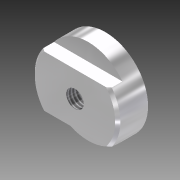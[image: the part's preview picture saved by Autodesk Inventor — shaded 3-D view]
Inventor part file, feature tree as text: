
AUTODESK INVENTOR PART (.ipt)
format: ipt  version: 2011 (Build 150239000, 239)  size: 103,936 bytes
history: native  units: in
note: dims shown in document units (in); Inventor stores cm internally (conversion verified against a paired STEP export)
features: extrude x3, sketch x3, chamfer x1, thread x1
ambient origin geometry x8: Origin, YZ Plane, XZ Plane, XY Plane, X Axis, Y Axis, Z Axis, Center Point
bodies: Solid1 (feature_tree)
feature tree (8):
  extrude  "Extrusion1"  Depth=0.737in TaperAngle=0.0deg
  chamfer  "Chamfer1"  Distance=0.0625in Angle=45.0deg
  extrude  "Extrusion2"  Depth=0.625in
  extrude  "Extrusion3"  Depth=0.425in
  thread  "Thread1"  [1 undecoded]
  sketch  "Sketch1"  dims[d0=2.082in d1=0.737in d2=0.0in d3=0.0625in d4=0.125in d5=45.0deg]
  sketch  "Sketch2"  dims[d6=1.25in d7=0.625in]
  sketch  "Sketch3"  dims[d8=0.32in d9=0.0in d10=0.425in d11=0.32in d12=0.0in d13=1.0in d14=0.0in]
note: 1 required parameter value undecoded (feature->parameter linkage not recoverable at this tier; creation-order binding heuristic only, values carry confidence <= 0.55)
